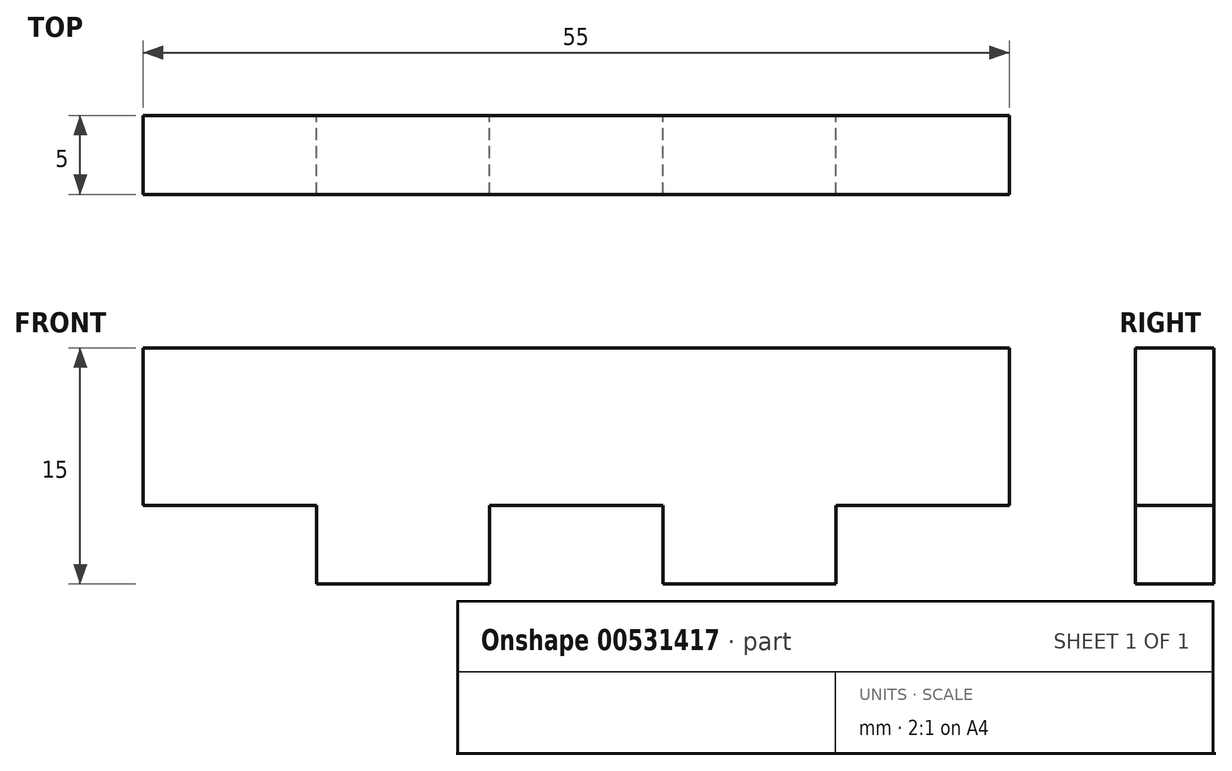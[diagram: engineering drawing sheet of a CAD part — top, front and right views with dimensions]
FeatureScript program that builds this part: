
annotation { "Feature Type Name" : "Feature", "Feature Type Description" : "" }
export const myFeature = defineFeature(function(context is Context, id is Id, definition is map)
    precondition{}
    {
        {
            var Q0;
            Q0=qCreatedBy(makeId("Front.planeOp"),FACE);
            var sketch = newSketch(context, id + "F0", { "sketchPlane" : qUnion([Q0])});
            skLineSegment(sketch, "E0.bottom", {"start": v(27.5, 5) * mm, "end": v(-27.5, 5) * mm});
            skLineSegment(sketch, "E0.top", {"start": v(27.5, -5) * mm, "end": v(16.5, -5) * mm});
            skLineSegment(sketch, "E0.left", {"start": v(27.5, 5) * mm, "end": v(27.5, -5) * mm});
            skLineSegment(sketch, "E0.right", {"start": v(-27.5, 5) * mm, "end": v(-27.5, -5) * mm});
            skPoint(sketch, "E0.middle", {"position": v(0, 0) * mm});
            skLineSegment(sketch, "E1", {"start": v(-27.5, 5) * mm, "end": v(-32.5, 5) * mm, "construction": true});
            skLineSegment(sketch, "E2", {"start": v(-32.5, 5) * mm, "end": v(-32.5, -10) * mm, "construction": true});
            skLineSegment(sketch, "E3", {"start": v(-32.5, -10) * mm, "end": v(32.5, -10) * mm, "construction": true});
            skLineSegment(sketch, "E4", {"start": v(32.5, -10) * mm, "end": v(32.5, 5) * mm, "construction": true});
            skLineSegment(sketch, "E5", {"start": v(32.5, 5) * mm, "end": v(27.5, 5) * mm, "construction": true});
            skLineSegment(sketch, "E6.top", {"start": v(-16.5, -10) * mm, "end": v(-5.5, -10) * mm});
            skLineSegment(sketch, "E6.left", {"start": v(-16.5, -5) * mm, "end": v(-16.5, -10) * mm});
            skLineSegment(sketch, "E6.right", {"start": v(-5.5, -5) * mm, "end": v(-5.5, -10) * mm});
            skLineSegment(sketch, "E7.top", {"start": v(5.5, -10) * mm, "end": v(16.5, -10) * mm});
            skLineSegment(sketch, "E7.left", {"start": v(5.5, -5) * mm, "end": v(5.5, -10) * mm});
            skLineSegment(sketch, "E7.right", {"start": v(16.5, -5) * mm, "end": v(16.5, -10) * mm});
            skLineSegment(sketch, "E8.trimOffspring", {"start": v(-16.5, -5) * mm, "end": v(-27.5, -5) * mm});
            skLineSegment(sketch, "E9.trimOffspring", {"start": v(5.5, -5) * mm, "end": v(-5.5, -5) * mm});
            skSolve(sketch);
        }
        {
            var Q0;
            Q0 = qSketchRegion(id + "F0", true);
            extrude(context, id + "F1", {"entities" : qUnion([Q0]), "depth" : 5 * mm, "offsetDistance" : 25 * mm});
        }
    });
